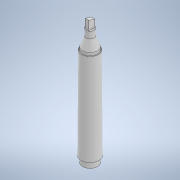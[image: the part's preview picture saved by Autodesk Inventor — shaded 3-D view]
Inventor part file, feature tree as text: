
AUTODESK INVENTOR PART (.ipt)
format: ipt  version: 2022 (Build 260153000, 153)  size: 160,256 bytes
history: native  units: mm
features: sketch x9, extrude x6, other x2, plane x2, loft x2
ambient origin geometry x8: Origin, YZ Plane, XZ Plane, XY Plane, X Axis, Y Axis, Z Axis, Center Point
bodies: Body1 (feature_tree)
feature tree (21):
  other  "Sólido1"
  extrude  "Extrusión1"  Depth=17.4mm
  sketch  "Boceto2"  dims[d2=5.9mm d3=0.0mm d5=17.4mm]
  plane  "Plano de trabajo1"
  loft  "Solevación1"
  extrude  "Extrusión2"  Depth=16.23mm
  extrude  "Extrusión3"  TaperAngle=0.0deg  [1 undecoded]
  plane  "Plano de trabajo2"
  loft  "Solevación2"
  extrude  "Extrusión4"  Depth=2.65mm TaperAngle=0.0deg
  extrude  "Extrusión5"  Depth=7.9mm
  extrude  "Extrusión6"  TaperAngle=0.0deg  [1 undecoded]
  sketch  "Boceto1"  dims[d0=14.55mm d1=17.4mm]
  sketch  "Boceto3"  dims[d6=-95.1mm d7=16.23mm]
  sketch  "Boceto4"  dims[d8=0.0mm d9=90.0deg d10=0.0mm d11=90.0deg]
  sketch  "Boceto5"  dims[d12=13.03mm d13=1.08mm d14=0.0mm]
  sketch  "Boceto6"  dims[d15=14.42mm d16=2.65mm d17=0.0mm]
  other  "Aristas1"
  sketch  "Boceto7"  dims[d18=9.15mm d19=7.9mm]
  sketch  "Boceto8"  dims[d20=0.0mm d21=90.0deg d22=0.0mm d23=90.0deg]
  sketch  "Boceto9"  dims[d24=6.58mm d25=0.0mm d26=3.6mm d27=5.56mm d28=8.65mm d29=0.0mm d30=7.0mm d31=8.65mm d32=0.0mm]
note: 2 required parameter values undecoded (feature->parameter linkage not recoverable at this tier; creation-order binding heuristic only, values carry confidence <= 0.55)
